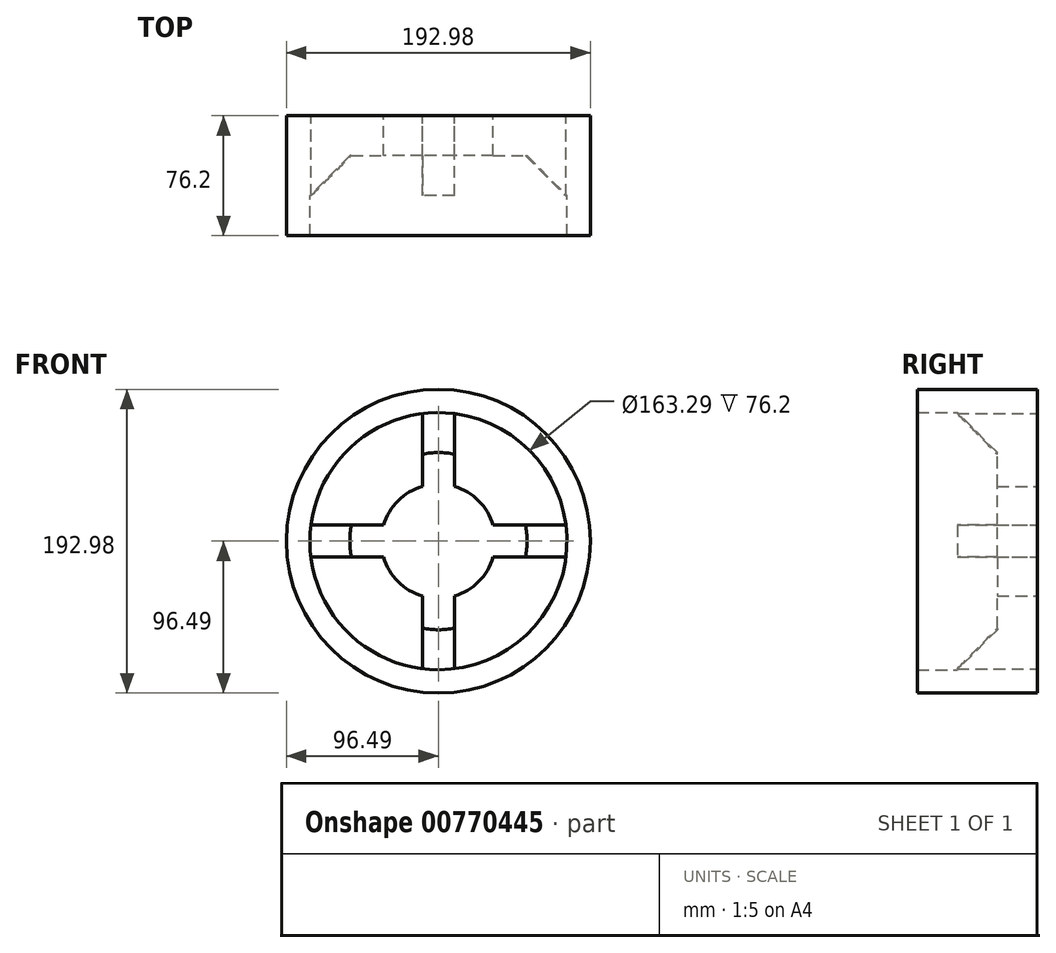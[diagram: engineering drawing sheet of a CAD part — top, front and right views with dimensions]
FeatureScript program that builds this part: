
annotation { "Feature Type Name" : "Feature", "Feature Type Description" : "" }
export const myFeature = defineFeature(function(context is Context, id is Id, definition is map)
    precondition{}
    {
        {
            var Q0;
            Q0=qCreatedBy(makeId("Front.planeOp"),FACE);
            var sketch = newSketch(context, id + "F0", { "sketchPlane" : qUnion([Q0])});
            skCircle(sketch, "E0", {"center": v(0, 0) * mm, "radius": 96.5 * mm});
            skCircle(sketch, "E1", {"center": v(0, 0) * mm, "radius": 81.64 * mm});
            skSolve(sketch);
        }
        {
            var Q0;
            Q0=makeQuery(id+"F0.imprint","IMPRINT",FACE,{"disambiguationData":[TD([[makeQuery(id+"F0.imprint","IMPRINT",EDGE,{"derivedFrom":sQuery(id+"F0.wireOp",EDGE,"E0")}),1.0]])]});
            extrude(context, id + "F1", {"entities" : qUnion([Q0]), "depth" : 76.2 * mm, "offsetDistance" : 25.4 * mm});
        }
        {
            var Q0;
            Q0=qCreatedBy(makeId("Front.planeOp"),FACE);
            var sketch = newSketch(context, id + "F2", { "sketchPlane" : qUnion([Q0])});
            skLineSegment(sketch, "E2.bottom", {"start": v(-90.17, -10.16) * mm, "end": v(90.17, -10.16) * mm});
            skLineSegment(sketch, "E2.top", {"start": v(-90.17, 10.16) * mm, "end": v(90.17, 10.16) * mm});
            skLineSegment(sketch, "E2.left", {"start": v(-90.17, -10.16) * mm, "end": v(-90.17, 10.16) * mm});
            skLineSegment(sketch, "E2.right", {"start": v(90.17, -10.16) * mm, "end": v(90.17, 10.16) * mm});
            skPoint(sketch, "E2.middle", {"position": v(0, 0) * mm});
            skLineSegment(sketch, "E3.bottom", {"start": v(-10.16, -90.17) * mm, "end": v(10.16, -90.17) * mm});
            skLineSegment(sketch, "E3.top", {"start": v(-10.16, 90.17) * mm, "end": v(10.16, 90.17) * mm});
            skLineSegment(sketch, "E3.left", {"start": v(-10.16, -90.17) * mm, "end": v(-10.16, 90.17) * mm});
            skLineSegment(sketch, "E3.right", {"start": v(10.16, -90.17) * mm, "end": v(10.16, 90.17) * mm});
            skSolve(sketch);
        }
        {
            var Q0;
            Q0 = qSketchRegion(id + "F2", true);
            extrude(context, id + "F3", {"entities" : qUnion([Q0]), "operationType" : NewBodyOperationType.ADD, "depth" : 25.4 * mm, "offsetDistance" : 25.4 * mm});
        }
        {
            var Q0;
            Q0=qCreatedBy(makeId("Front.planeOp"),FACE);
            var sketch = newSketch(context, id + "F4", { "sketchPlane" : qUnion([Q0])});
            skCircle(sketch, "E4", {"center": v(0, 0) * mm, "radius": 36.26 * mm});
            skSolve(sketch);
        }
        {
            var Q0;
            Q0 = qSketchRegion(id + "F4", true);
            extrude(context, id + "F5", {"entities" : qUnion([Q0]), "operationType" : NewBodyOperationType.ADD, "depth" : 25.4 * mm, "offsetDistance" : 25.4 * mm});
        }
        {
            var Q0;
            Q0=makeQuery(id+"F3.boolean.opBoolean","INTERSECT",EDGE,{"disambiguationData":[OD(2.0)],"derivedFrom":[makeQuery(id+"F1.opExtrude","SWEPT_FACE",FACE,{"disambiguationData":[OSD([sQuery(id+"F0.wireOp",EDGE,"E1")])]}),makeQuery(id+"F3.opExtrude","CAP_FACE",FACE,{"disambiguationData":[OSD([sQuery(id+"F2.wireOp",EDGE,"E2.bottom"),sQuery(id+"F2.wireOp",EDGE,"E2.top"),sQuery(id+"F2.wireOp",EDGE,"E2.left"),sQuery(id+"F2.wireOp",EDGE,"E2.right"),sQuery(id+"F2.wireOp",EDGE,"E3.bottom"),sQuery(id+"F2.wireOp",EDGE,"E3.top"),sQuery(id+"F2.wireOp",EDGE,"E3.left"),sQuery(id+"F2.wireOp",EDGE,"E3.right")])],"isStart":false})]});
            var Q1;
            Q1=makeQuery(id+"F3.boolean.opBoolean","INTERSECT",EDGE,{"disambiguationData":[OD(0.0)],"derivedFrom":[makeQuery(id+"F1.opExtrude","SWEPT_FACE",FACE,{"disambiguationData":[OSD([sQuery(id+"F0.wireOp",EDGE,"E1")])]}),makeQuery(id+"F3.opExtrude","CAP_FACE",FACE,{"disambiguationData":[OSD([sQuery(id+"F2.wireOp",EDGE,"E2.bottom"),sQuery(id+"F2.wireOp",EDGE,"E2.top"),sQuery(id+"F2.wireOp",EDGE,"E2.left"),sQuery(id+"F2.wireOp",EDGE,"E2.right"),sQuery(id+"F2.wireOp",EDGE,"E3.bottom"),sQuery(id+"F2.wireOp",EDGE,"E3.top"),sQuery(id+"F2.wireOp",EDGE,"E3.left"),sQuery(id+"F2.wireOp",EDGE,"E3.right")])],"isStart":false})]});
            var Q2;
            Q2=makeQuery(id+"F3.boolean.opBoolean","INTERSECT",EDGE,{"disambiguationData":[OD(1.0)],"derivedFrom":[makeQuery(id+"F1.opExtrude","SWEPT_FACE",FACE,{"disambiguationData":[OSD([sQuery(id+"F0.wireOp",EDGE,"E1")])]}),makeQuery(id+"F3.opExtrude","CAP_FACE",FACE,{"disambiguationData":[OSD([sQuery(id+"F2.wireOp",EDGE,"E2.bottom"),sQuery(id+"F2.wireOp",EDGE,"E2.top"),sQuery(id+"F2.wireOp",EDGE,"E2.left"),sQuery(id+"F2.wireOp",EDGE,"E2.right"),sQuery(id+"F2.wireOp",EDGE,"E3.bottom"),sQuery(id+"F2.wireOp",EDGE,"E3.top"),sQuery(id+"F2.wireOp",EDGE,"E3.left"),sQuery(id+"F2.wireOp",EDGE,"E3.right")])],"isStart":false})]});
            var Q3;
            Q3=makeQuery(id+"F3.boolean.opBoolean","INTERSECT",EDGE,{"disambiguationData":[OD(3.0)],"derivedFrom":[makeQuery(id+"F1.opExtrude","SWEPT_FACE",FACE,{"disambiguationData":[OSD([sQuery(id+"F0.wireOp",EDGE,"E1")])]}),makeQuery(id+"F3.opExtrude","CAP_FACE",FACE,{"disambiguationData":[OSD([sQuery(id+"F2.wireOp",EDGE,"E2.bottom"),sQuery(id+"F2.wireOp",EDGE,"E2.top"),sQuery(id+"F2.wireOp",EDGE,"E2.left"),sQuery(id+"F2.wireOp",EDGE,"E2.right"),sQuery(id+"F2.wireOp",EDGE,"E3.bottom"),sQuery(id+"F2.wireOp",EDGE,"E3.top"),sQuery(id+"F2.wireOp",EDGE,"E3.left"),sQuery(id+"F2.wireOp",EDGE,"E3.right")])],"isStart":false})]});
            chamfer(context, id + "F6", {"entities" : qUnion([Q0, Q1, Q2, Q3]), "width" : 25.4 * mm, "tangentPropagation" : true});
        }
    });
